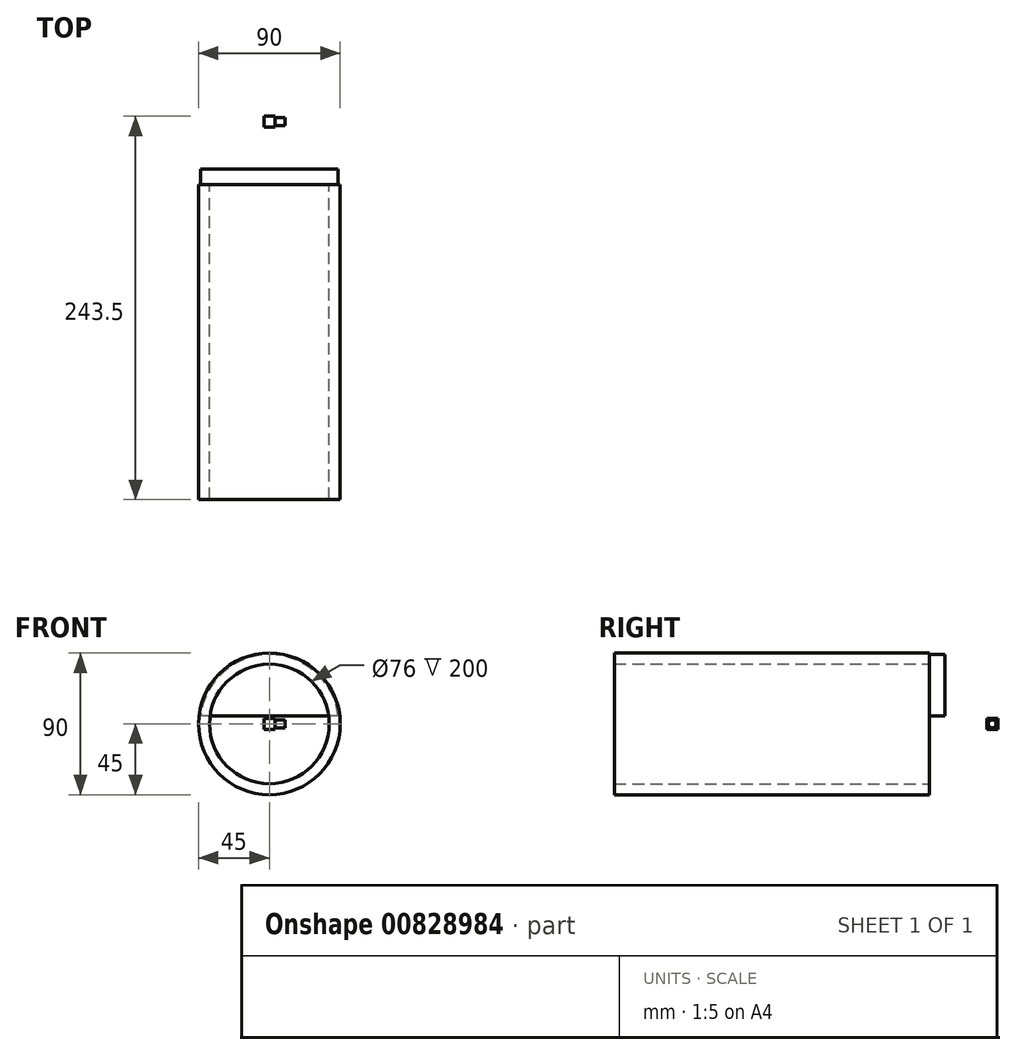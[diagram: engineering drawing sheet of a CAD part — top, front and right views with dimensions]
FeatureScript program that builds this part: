
annotation { "Feature Type Name" : "Feature", "Feature Type Description" : "" }
export const myFeature = defineFeature(function(context is Context, id is Id, definition is map)
    precondition{}
    {
        {
            var Q0;
            Q0=qCreatedBy(makeId("Front.planeOp"),FACE);
            var sketch = newSketch(context, id + "F0", { "sketchPlane" : qUnion([Q0])});
            skCircle(sketch, "E0", {"center": v(0, 0) * mm, "radius": 45 * mm});
            skCircle(sketch, "E1", {"center": v(0, 0) * mm, "radius": 38 * mm});
            skSolve(sketch);
        }
        {
            var Q0;
            Q0=qSketchRegion(id+"F0",true);
            extrude(context, id + "F1", {"entities" : qUnion([Q0]), "depth" : 200 * mm, "offsetDistance" : 25 * mm});
        }
        {
            var Q0;
            Q0=qCreatedBy(makeId("Right.planeOp"),FACE);
            var sketch = newSketch(context, id + "F2", { "sketchPlane" : qUnion([Q0])});
            skLineSegment(sketch, "E2", {"start": v(0, 0) * mm, "end": v(40, 0) * mm});
            skCircle(sketch, "E3", {"center": v(40, 0) * mm, "radius": 2.5 * mm});
            skSolve(sketch);
        }
        {
            var Q0;
            Q0=makeQuery(id+"F2.imprint","IMPRINT",FACE,{"disambiguationData":[TD([[makeQuery(id+"F2.imprint","IMPRINT",EDGE,{"derivedFrom":sQuery(id+"F2.wireOp",EDGE,"E3")}),1.0]])]});
            extrude(context, id + "F3", {"entities" : qUnion([Q0]), "depth" : 10 * mm, "offsetDistance" : 25 * mm});
        }
        {
            var Q0;
            Q0=makeQuery(id+"F1.opExtrude","CAP_FACE",FACE,{"disambiguationData":[OSD([sQuery(id+"F0.wireOp",EDGE,"E0"),sQuery(id+"F0.wireOp",EDGE,"E1")])],"isStart":true});
            var sketch = newSketch(context, id + "F4", { "sketchPlane" : qUnion([Q0])});
            skLineSegment(sketch, "E4", {"start": v(0, 0) * mm, "end": v(0, 5) * mm});
            skLineSegment(sketch, "E5", {"start": v(0, 5) * mm, "end": v(43.71, 5) * mm});
            skLineSegment(sketch, "E6", {"start": v(0, 5) * mm, "end": v(-43.71, 5) * mm});
            skCircle(sketch, "E7", {"center": v(0, 0) * mm, "radius": 44 * mm});
            skSolve(sketch);
        }
        {
            var Q0;
            {var subQ0=sQuery(id+"F4.wireOp",EDGE,"E7");var subQ1=sQuery(id+"F4.wireOp",EDGE,"E5");var subQ2=makeQuery(id+"F4.imprint","INTERSECT",VERTEX,{"derivedFrom":[subQ1,subQ0]});Q0=makeQuery(id+"F4.imprint","IMPRINT",FACE,{"disambiguationData":[TD([[makeQuery(id+"F4.imprint","IMPRINT",EDGE,{"disambiguationData":[TD([[subQ2,1.0]])],"derivedFrom":subQ1}),1.0]])]});}
            var Q1;
            {var subQ0=sQuery(id+"F4.wireOp",EDGE,"E6");var subQ1=sQuery(id+"F4.wireOp",EDGE,"E5");var subQ2=makeQuery(id+"F4.imprint","INTERSECT",VERTEX,{"derivedFrom":[subQ1,subQ0]});Q1=makeQuery(id+"F4.imprint","IMPRINT",FACE,{"disambiguationData":[TD([[makeQuery(id+"F4.imprint","IMPRINT",EDGE,{"disambiguationData":[TD([[subQ2,-1.0]])],"derivedFrom":subQ1}),1.0]])]});}
            extrude(context, id + "F5", {"entities" : qUnion([Q0, Q1]), "depth" : 10 * mm, "offsetDistance" : 25 * mm});
        }
        {
            var Q0;
            Q0=qCreatedBy(makeId("Right.planeOp"),FACE);
            var sketch = newSketch(context, id + "F6", { "sketchPlane" : qUnion([Q0])});
            skLineSegment(sketch, "E8", {"start": v(0, 0) * mm, "end": v(40, 0) * mm});
            skLineSegment(sketch, "E9.bottom", {"start": v(36.5, -3.5) * mm, "end": v(43.5, -3.5) * mm});
            skLineSegment(sketch, "E9.top", {"start": v(36.5, 3.5) * mm, "end": v(43.5, 3.5) * mm});
            skLineSegment(sketch, "E9.left", {"start": v(36.5, -3.5) * mm, "end": v(36.5, 3.5) * mm});
            skLineSegment(sketch, "E9.right", {"start": v(43.5, -3.5) * mm, "end": v(43.5, 3.5) * mm});
            skPoint(sketch, "E9.middle", {"position": v(40, 0) * mm});
            skSolve(sketch);
        }
        {
            var Q0;
            {var subQ0=sQuery(id+"F6.wireOp",EDGE,"E9.bottom");Q0=makeQuery(id+"F6.imprint","IMPRINT",FACE,{"disambiguationData":[TD([[makeQuery(id+"F6.imprint","IMPRINT",EDGE,{"derivedFrom":subQ0}),1.0]])]});}
            extrude(context, id + "F7", {"entities" : qUnion([Q0]), "operationType" : NewBodyOperationType.ADD, "endBound" : BoundingType.SYMMETRIC, "depth" : 7 * mm, "offsetDistance" : 25 * mm});
        }
    });
